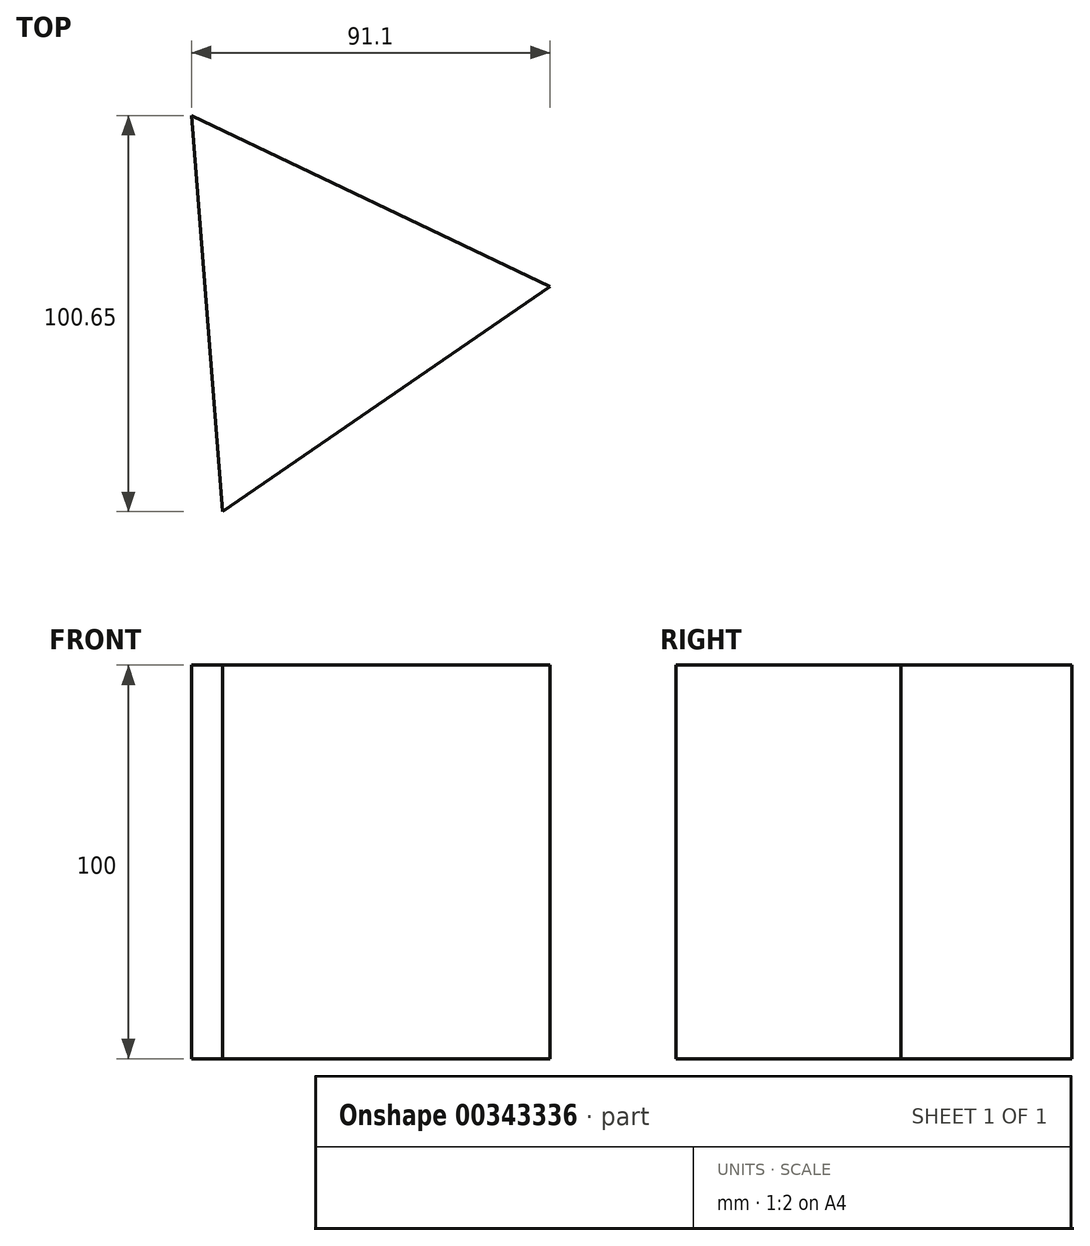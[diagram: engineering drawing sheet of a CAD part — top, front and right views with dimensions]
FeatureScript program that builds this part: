
annotation { "Feature Type Name" : "Feature", "Feature Type Description" : "" }
export const myFeature = defineFeature(function(context is Context, id is Id, definition is map)
    precondition{}
    {
        {
            var Q0;
            Q0=qCreatedBy(makeId("Top.planeOp"),FACE);
            var sketch = newSketch(context, id + "F0", { "sketchPlane" : qUnion([Q0])});
            skCircle(sketch, "E0.cCircle", {"center": v(0, 0) * mm, "radius": 58.29 * mm, "construction": true});
            skLineSegment(sketch, "E0.0", {"start": v(-33, 48.05) * mm, "end": v(58.11, 4.55) * mm});
            skLineSegment(sketch, "E0.1", {"start": v(58.11, 4.55) * mm, "end": v(-25.12, -52.6) * mm});
            skLineSegment(sketch, "E0.2", {"start": v(-25.12, -52.6) * mm, "end": v(-33, 48.05) * mm});
            skSolve(sketch);
        }
        {
            var Q0;
            Q0=makeQuery(id+"F0.imprint","IMPRINT",FACE,{"disambiguationData":[TD([[makeQuery(id+"F0.imprint","IMPRINT",EDGE,{"derivedFrom":sQuery(id+"F0.wireOp",EDGE,"E0.0")}),-1.0]])]});
            extrude(context, id + "F1", {"entities" : qUnion([Q0]), "depth" : 100 * mm});
        }
    });
